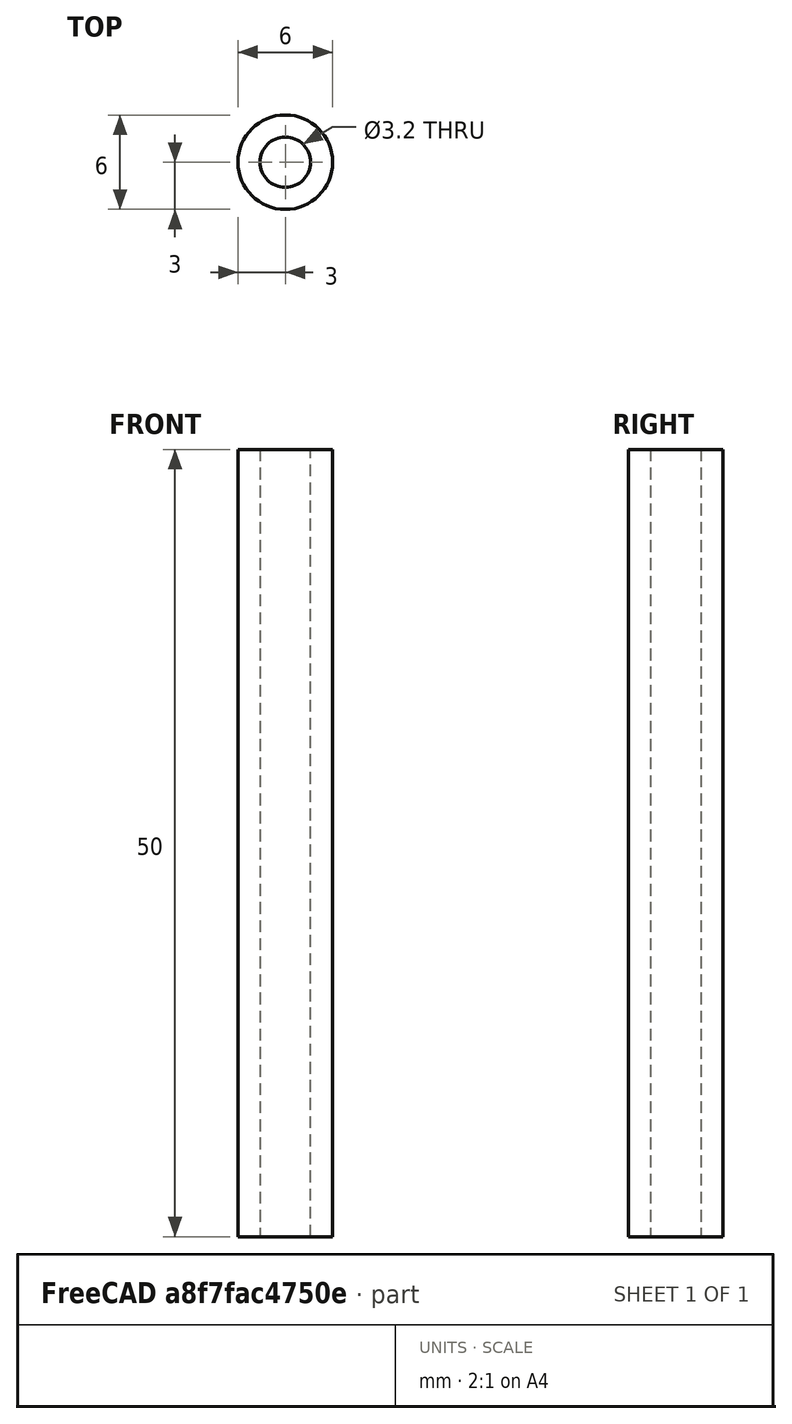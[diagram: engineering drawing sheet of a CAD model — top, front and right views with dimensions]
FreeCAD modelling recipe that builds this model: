
FCSTD DOCUMENT  (FreeCAD 1.0R39109 (Git))
Label: 50mm_spacer
License: All rights reserved
LicenseURL: https://en.wikipedia.org/wiki/All_rights_reserved
objects: Sketcher::SketchObject×1, PartDesign::Pad×1, PartDesign::Body×1
note: 6 computed .brp shape members not serialized (recipe doc carries the construction recipe); baked Part::Feature solids carry a one-line shape summary decoded from their .brp

FEATURE [Sketcher::SketchObject] Sketch
  ArcFitTolerance = 1e-06
  AttachmentSupport = -> [XY_Plane]
  FullyConstrained = true
  MakeInternals = false
  MapMode = 5
  sketch-geometry (2):
    g0: Circle CenterX=0 CenterY=0 CenterZ=0 NormalX=0 NormalY=0 NormalZ=1 AngleXU=0 Radius=1.6
    g1: Circle CenterX=0 CenterY=0 CenterZ=0 NormalX=0 NormalY=0 NormalZ=1 AngleXU=0 Radius=3
  constraints (4):
    c: Coincident(g0,g-1)
    c: Coincident(g1,g0)
    c: Diameter(g0) = 3.2
    c: Diameter(g1) = 6
FEATURE [PartDesign::Pad] Pad
  Direction = (0,0,1)
  Length = 50
  Length2 = 10
  Profile = -> Sketch
  ReferenceAxis = -> Sketch [N_Axis]
  Refine = true
  Suppressed = false
  Type = 0
FEATURE [PartDesign::Body] Body
  AllowCompound = false
  Group = -> [Sketch,Pad]
  Origin = -> Origin
  Tip = -> Pad
